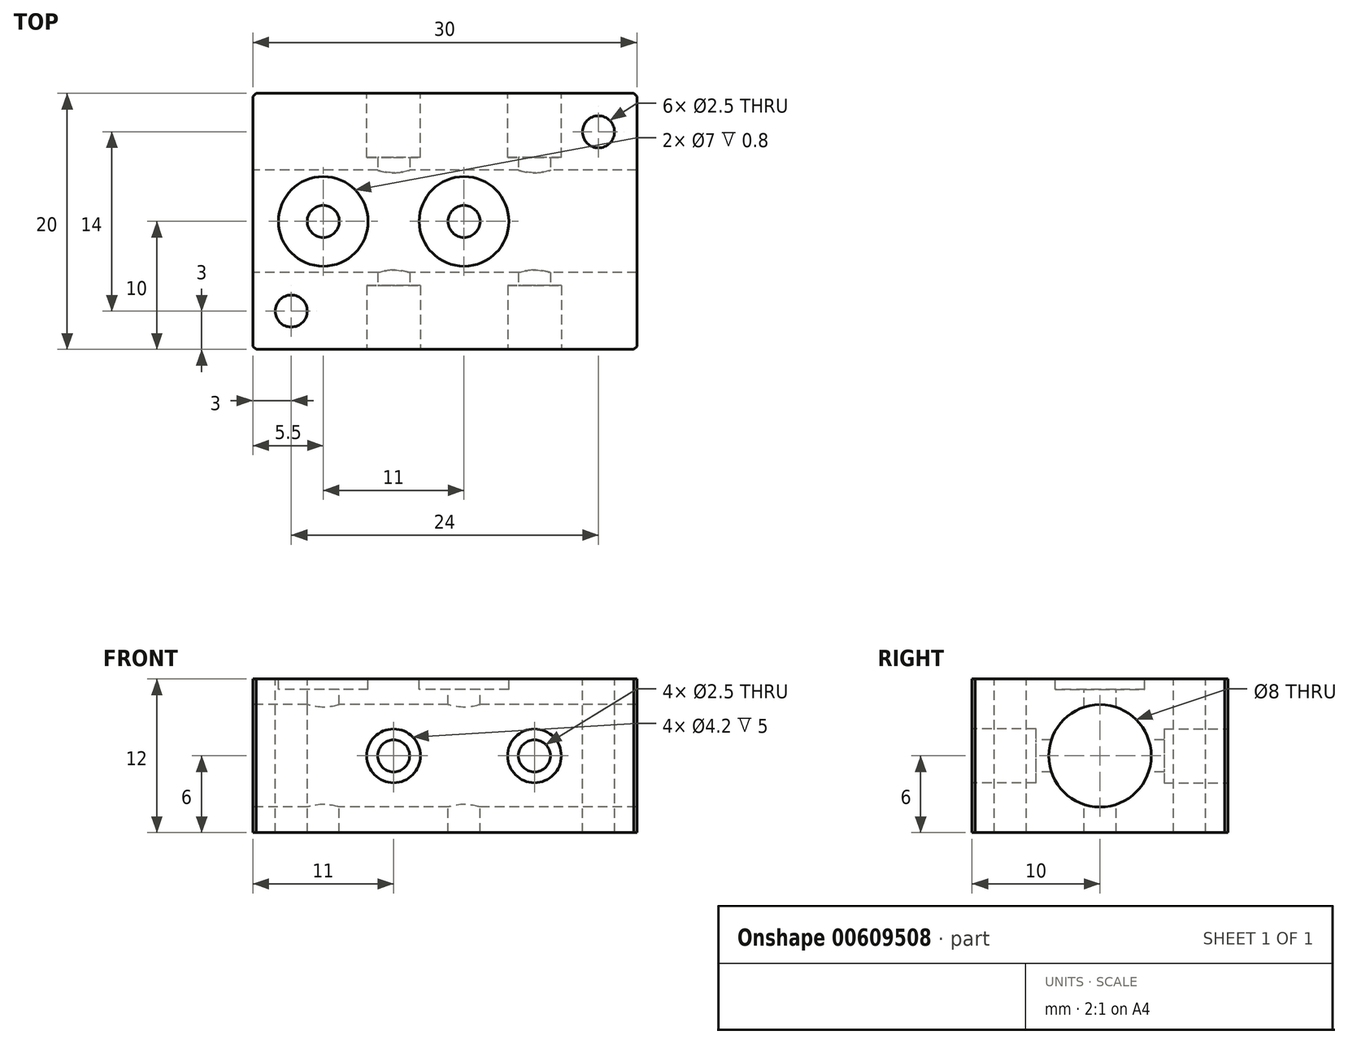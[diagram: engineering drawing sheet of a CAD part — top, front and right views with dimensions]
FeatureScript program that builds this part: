
annotation { "Feature Type Name" : "Feature", "Feature Type Description" : "" }
export const myFeature = defineFeature(function(context is Context, id is Id, definition is map)
    precondition{}
    {
        {
            var Q0;
            Q0=qCreatedBy(makeId("Top.planeOp"),FACE);
            var sketch = newSketch(context, id + "F0", { "sketchPlane" : qUnion([Q0])});
            skLineSegment(sketch, "E0.bottom", {"start": v(0, 0) * mm, "end": v(30, 0) * mm});
            skLineSegment(sketch, "E0.top", {"start": v(0, -20) * mm, "end": v(30, -20) * mm});
            skLineSegment(sketch, "E0.left", {"start": v(0, 0) * mm, "end": v(0, -20) * mm});
            skLineSegment(sketch, "E0.right", {"start": v(30, 0) * mm, "end": v(30, -20) * mm});
            skSolve(sketch);
        }
        {
            var Q0;
            Q0=makeQuery(id+"F0.imprint","IMPRINT",FACE,{"disambiguationData":[TD([[makeQuery(id+"F0.imprint","IMPRINT",EDGE,{"derivedFrom":sQuery(id+"F0.wireOp",EDGE,"E0.bottom")}),-1.0]])]});
            extrude(context, id + "F1", {"entities" : qUnion([Q0]), "depth" : 12 * mm, "offsetDistance" : 25 * mm});
        }
        {
            var Q0;
            Q0=makeQuery(id+"F1.opExtrude","SWEPT_FACE",FACE,{"disambiguationData":[OSD([sQuery(id+"F0.wireOp",EDGE,"E0.top")])]});
            var sketch = newSketch(context, id + "F2", { "sketchPlane" : qUnion([Q0])});
            skLineSegment(sketch, "E1", {"start": v(30, 6) * mm, "end": v(0, 6) * mm, "construction": true});
            skCircle(sketch, "E2", {"center": v(22, 6) * mm, "radius": 2.1 * mm});
            skCircle(sketch, "E3", {"center": v(11, 6) * mm, "radius": 2.1 * mm});
            skCircle(sketch, "E4", {"center": v(11, 6) * mm, "radius": 1.25 * mm});
            skCircle(sketch, "E5", {"center": v(22, 6) * mm, "radius": 1.25 * mm});
            skSolve(sketch);
        }
        {
            var Q0;
            Q0=makeQuery(id+"F2.imprint","IMPRINT",FACE,{"disambiguationData":[TD([[makeQuery(id+"F2.imprint","IMPRINT",EDGE,{"derivedFrom":sQuery(id+"F2.wireOp",EDGE,"E4")}),1.0]])]});
            var Q1;
            Q1=makeQuery(id+"F2.imprint","IMPRINT",FACE,{"disambiguationData":[TD([[makeQuery(id+"F2.imprint","IMPRINT",EDGE,{"derivedFrom":sQuery(id+"F2.wireOp",EDGE,"E5")}),1.0]])]});
            extrude(context, id + "F3", {"entities" : qUnion([Q0, Q1]), "operationType" : NewBodyOperationType.REMOVE, "oppositeDirection" : true, "depth" : 25 * mm, "offsetDistance" : 25 * mm});
        }
        {
            var Q0;
            Q0=makeQuery(id+"F1.opExtrude","SWEPT_FACE",FACE,{"disambiguationData":[OSD([sQuery(id+"F0.wireOp",EDGE,"E0.bottom")])]});
            var sketch = newSketch(context, id + "F4", { "sketchPlane" : qUnion([Q0])});
            skCircle(sketch, "E6", {"center": v(-11, 6) * mm, "radius": 2.1 * mm});
            skCircle(sketch, "E7", {"center": v(-22, 6) * mm, "radius": 2.1 * mm});
            skSolve(sketch);
        }
        {
            var Q0;
            Q0=makeQuery(id+"F4.imprint","IMPRINT",FACE,{"disambiguationData":[TD([[makeQuery(id+"F4.imprint","IMPRINT",EDGE,{"derivedFrom":sQuery(id+"F4.wireOp",EDGE,"E6")}),1.0]])]});
            var Q1;
            Q1=makeQuery(id+"F4.imprint","IMPRINT",FACE,{"disambiguationData":[TD([[makeQuery(id+"F4.imprint","IMPRINT",EDGE,{"derivedFrom":sQuery(id+"F4.wireOp",EDGE,"E7")}),1.0]])]});
            extrude(context, id + "F5", {"entities" : qUnion([Q0, Q1]), "operationType" : NewBodyOperationType.REMOVE, "oppositeDirection" : true, "depth" : 5 * mm, "offsetDistance" : 25 * mm});
        }
        {
            var Q0;
            Q0=makeQuery(id+"F2.imprint","IMPRINT",FACE,{"disambiguationData":[TD([[makeQuery(id+"F2.imprint","IMPRINT",EDGE,{"derivedFrom":sQuery(id+"F2.wireOp",EDGE,"E2")}),1.0]])]});
            var Q1;
            Q1=makeQuery(id+"F2.imprint","IMPRINT",FACE,{"disambiguationData":[TD([[makeQuery(id+"F2.imprint","IMPRINT",EDGE,{"derivedFrom":sQuery(id+"F2.wireOp",EDGE,"E3")}),1.0]])]});
            extrude(context, id + "F6", {"entities" : qUnion([Q0, Q1]), "operationType" : NewBodyOperationType.REMOVE, "oppositeDirection" : true, "depth" : 5 * mm, "offsetDistance" : 25 * mm});
        }
        {
            var Q0;
            Q0=makeQuery(id+"F1.opExtrude","SWEPT_FACE",FACE,{"disambiguationData":[OSD([sQuery(id+"F0.wireOp",EDGE,"E0.left")])]});
            var sketch = newSketch(context, id + "F7", { "sketchPlane" : qUnion([Q0])});
            skLineSegment(sketch, "E8", {"start": v(0, 6) * mm, "end": v(20, 6) * mm, "construction": true});
            skCircle(sketch, "E9", {"center": v(10, 6) * mm, "radius": 4 * mm});
            skSolve(sketch);
        }
        {
            var Q0;
            Q0=makeQuery(id+"F7.imprint","IMPRINT",FACE,{"disambiguationData":[TD([[makeQuery(id+"F7.imprint","IMPRINT",EDGE,{"derivedFrom":sQuery(id+"F7.wireOp",EDGE,"E9")}),1.0]])]});
            extrude(context, id + "F8", {"entities" : qUnion([Q0]), "operationType" : NewBodyOperationType.REMOVE, "oppositeDirection" : true, "depth" : 30 * mm, "offsetDistance" : 25 * mm});
        }
        {
            var Q0;
            Q0=makeQuery(id+"F1.opExtrude","CAP_FACE",FACE,{"disambiguationData":[OSD([sQuery(id+"F0.wireOp",EDGE,"E0.bottom"),sQuery(id+"F0.wireOp",EDGE,"E0.top"),sQuery(id+"F0.wireOp",EDGE,"E0.left"),sQuery(id+"F0.wireOp",EDGE,"E0.right")])],"isStart":false});
            var sketch = newSketch(context, id + "F9", { "sketchPlane" : qUnion([Q0])});
            skLineSegment(sketch, "E10", {"start": v(30, -10) * mm, "end": v(0, -10) * mm, "construction": true});
            skCircle(sketch, "E11", {"center": v(16.5, -10) * mm, "radius": 1.25 * mm});
            skCircle(sketch, "E12", {"center": v(5.5, -10) * mm, "radius": 1.25 * mm});
            skCircle(sketch, "E13", {"center": v(16.5, -10) * mm, "radius": 3.5 * mm});
            skCircle(sketch, "E14", {"center": v(5.5, -10) * mm, "radius": 3.5 * mm});
            skLineSegment(sketch, "E15", {"start": v(27, -20) * mm, "end": v(27, -3) * mm, "construction": true});
            skLineSegment(sketch, "E16", {"start": v(27, -3) * mm, "end": v(30, -3) * mm, "construction": true});
            skLineSegment(sketch, "E17", {"start": v(0, -17) * mm, "end": v(3, -17) * mm, "construction": true});
            skLineSegment(sketch, "E18", {"start": v(3, -17) * mm, "end": v(3, 0) * mm, "construction": true});
            skCircle(sketch, "E19", {"center": v(3, -17) * mm, "radius": 1.25 * mm});
            skCircle(sketch, "E20", {"center": v(27, -3) * mm, "radius": 1.25 * mm});
            skCircle(sketch, "E21", {"center": v(5.5, -10) * mm, "radius": 2.5 * mm});
            skCircle(sketch, "E22", {"center": v(16.5, -10) * mm, "radius": 2.5 * mm});
            skSolve(sketch);
        }
        {
            var Q0;
            Q0=makeQuery(id+"F9.imprint","IMPRINT",FACE,{"disambiguationData":[TD([[makeQuery(id+"F9.imprint","IMPRINT",EDGE,{"derivedFrom":sQuery(id+"F9.wireOp",EDGE,"E12")}),1.0]])]});
            var Q1;
            Q1=makeQuery(id+"F9.imprint","IMPRINT",FACE,{"disambiguationData":[TD([[makeQuery(id+"F9.imprint","IMPRINT",EDGE,{"derivedFrom":sQuery(id+"F9.wireOp",EDGE,"E11")}),1.0]])]});
            extrude(context, id + "F10", {"entities" : qUnion([Q0, Q1]), "operationType" : NewBodyOperationType.REMOVE, "oppositeDirection" : true, "depth" : 25 * mm, "offsetDistance" : 25 * mm});
        }
        {
            var Q0;
            Q0=makeQuery(id+"F1.opExtrude","CAP_FACE",FACE,{"disambiguationData":[OSD([sQuery(id+"F0.wireOp",EDGE,"E0.bottom"),sQuery(id+"F0.wireOp",EDGE,"E0.top"),sQuery(id+"F0.wireOp",EDGE,"E0.left"),sQuery(id+"F0.wireOp",EDGE,"E0.right")])],"isStart":true});
            var sketch = newSketch(context, id + "F11", { "sketchPlane" : qUnion([Q0])});
            skCircle(sketch, "E23", {"center": v(5.5, 10) * mm, "radius": 3 * mm});
            skCircle(sketch, "E24", {"center": v(16.5, 10) * mm, "radius": 3 * mm});
            skSolve(sketch);
        }
        {
            var Q0;
            Q0=makeQuery(id+"F1.opExtrude","CAP_FACE",FACE,{"disambiguationData":[OSD([sQuery(id+"F0.wireOp",EDGE,"E0.bottom"),sQuery(id+"F0.wireOp",EDGE,"E0.top"),sQuery(id+"F0.wireOp",EDGE,"E0.left"),sQuery(id+"F0.wireOp",EDGE,"E0.right")])],"isStart":true});
            var sketch = newSketch(context, id + "F12", { "sketchPlane" : qUnion([Q0])});
            skLineSegment(sketch, "E25.bottom", {"start": v(-8.36, -7.93) * mm, "end": v(37.73, -7.93) * mm});
            skLineSegment(sketch, "E25.top", {"start": v(-8.36, 26.65) * mm, "end": v(37.73, 26.65) * mm});
            skLineSegment(sketch, "E25.left", {"start": v(-8.36, -7.93) * mm, "end": v(-8.36, 26.65) * mm});
            skLineSegment(sketch, "E25.right", {"start": v(37.73, -7.93) * mm, "end": v(37.73, 26.65) * mm});
            skSolve(sketch);
        }
        {
            var Q0;
            Q0=makeQuery(id+"F9.imprint","IMPRINT",FACE,{"disambiguationData":[TD([[makeQuery(id+"F9.imprint","IMPRINT",EDGE,{"derivedFrom":sQuery(id+"F9.wireOp",EDGE,"E19")}),1.0]])]});
            var Q1;
            Q1=makeQuery(id+"F9.imprint","IMPRINT",FACE,{"disambiguationData":[TD([[makeQuery(id+"F9.imprint","IMPRINT",EDGE,{"derivedFrom":sQuery(id+"F9.wireOp",EDGE,"E20")}),1.0]])]});
            extrude(context, id + "F13", {"entities" : qUnion([Q0, Q1]), "operationType" : NewBodyOperationType.REMOVE, "oppositeDirection" : true, "depth" : 25 * mm, "offsetDistance" : 25 * mm});
        }
        {
            var Q0;
            Q0=makeQuery(id+"F8.boolean.opBoolean","COPY",EDGE,{"derivedFrom":makeQuery(id+"F8.opExtrude","CAP_EDGE",EDGE,{"disambiguationData":[OSD([sQuery(id+"F7.wireOp",EDGE,"E9")])],"isStart":true})});
            var Q1;
            Q1=makeQuery(id+"F5.boolean.opBoolean","COPY",EDGE,{"derivedFrom":makeQuery(id+"F5.opExtrude","CAP_EDGE",EDGE,{"disambiguationData":[OSD([sQuery(id+"F4.wireOp",EDGE,"E6")])],"isStart":true})});
            var Q2;
            Q2=makeQuery(id+"F5.boolean.opBoolean","COPY",EDGE,{"derivedFrom":makeQuery(id+"F5.opExtrude","CAP_EDGE",EDGE,{"disambiguationData":[OSD([sQuery(id+"F4.wireOp",EDGE,"E7")])],"isStart":true})});
            var Q3;
            Q3=makeQuery(id+"F6.boolean.opBoolean","COPY",EDGE,{"derivedFrom":makeQuery(id+"F6.opExtrude","CAP_EDGE",EDGE,{"disambiguationData":[OSD([sQuery(id+"F2.wireOp",EDGE,"E3")])],"isStart":true})});
            var Q4;
            Q4=makeQuery(id+"F6.boolean.opBoolean","COPY",EDGE,{"derivedFrom":makeQuery(id+"F6.opExtrude","CAP_EDGE",EDGE,{"disambiguationData":[OSD([sQuery(id+"F2.wireOp",EDGE,"E2")])],"isStart":true})});
            var Q5;
            Q5=makeQuery(id+"F1.opExtrude","SWEPT_EDGE",EDGE,{"disambiguationData":[OSD([sQuery(id+"F0.wireOp",EDGE,"E0.bottom"),sQuery(id+"F0.wireOp",EDGE,"E0.left")])]});
            var Q6;
            Q6=makeQuery(id+"F1.opExtrude","SWEPT_EDGE",EDGE,{"disambiguationData":[OSD([sQuery(id+"F0.wireOp",EDGE,"E0.top"),sQuery(id+"F0.wireOp",EDGE,"E0.left")])]});
            var Q7;
            Q7=makeQuery(id+"F1.opExtrude","SWEPT_EDGE",EDGE,{"disambiguationData":[OSD([sQuery(id+"F0.wireOp",EDGE,"E0.bottom"),sQuery(id+"F0.wireOp",EDGE,"E0.right")])]});
            var Q8;
            Q8=makeQuery(id+"F1.opExtrude","SWEPT_EDGE",EDGE,{"disambiguationData":[OSD([sQuery(id+"F0.wireOp",EDGE,"E0.top"),sQuery(id+"F0.wireOp",EDGE,"E0.right")])]});
            chamfer(context, id + "F14", {"entities" : qUnion([Q0, Q1, Q2, Q3, Q4, Q5, Q6, Q7, Q8]), "width" : 0.25 * mm, "tangentPropagation" : true});
        }
        {
            var Q0;
            Q0=makeQuery(id+"F9.imprint","IMPRINT",FACE,{"disambiguationData":[TD([[makeQuery(id+"F9.imprint","IMPRINT",EDGE,{"derivedFrom":sQuery(id+"F9.wireOp",EDGE,"E14")}),1.0]])]});
            var Q1;
            Q1=makeQuery(id+"F9.imprint","IMPRINT",FACE,{"disambiguationData":[TD([[makeQuery(id+"F9.imprint","IMPRINT",EDGE,{"derivedFrom":sQuery(id+"F9.wireOp",EDGE,"E13")}),1.0]])]});
            var Q2;
            Q2=makeQuery(id+"F9.imprint","IMPRINT",FACE,{"disambiguationData":[TD([[makeQuery(id+"F9.imprint","IMPRINT",EDGE,{"derivedFrom":sQuery(id+"F9.wireOp",EDGE,"E12")}),-1.0]])]});
            var Q3;
            Q3=makeQuery(id+"F9.imprint","IMPRINT",FACE,{"disambiguationData":[TD([[makeQuery(id+"F9.imprint","IMPRINT",EDGE,{"derivedFrom":sQuery(id+"F9.wireOp",EDGE,"E11")}),-1.0]])]});
            extrude(context, id + "F15", {"entities" : qUnion([Q0, Q1, Q2, Q3]), "operationType" : NewBodyOperationType.REMOVE, "flatOperationType" : FlatOperationType.REMOVE, "oppositeDirection" : true, "depth" : .8 * mm, "offsetDistance" : 25 * mm, "domain" : OperationDomain.MODEL});
        }
    });
